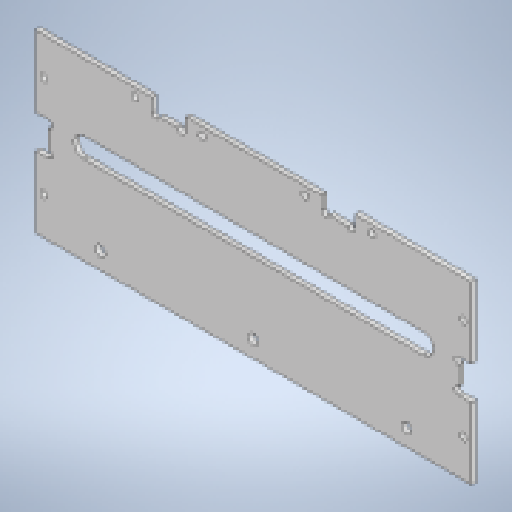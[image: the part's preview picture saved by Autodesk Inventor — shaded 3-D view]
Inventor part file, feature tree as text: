
AUTODESK INVENTOR PART (.ipt)
format: ipt  version: 2024 (Build 280153000, 153)  size: 256,000 bytes
history: native  units: mm
features: other x6, extrude x4, sketch x4, reference x3, projected_geometry x1
ambient origin geometry x8: Origin, YZ Plane, XZ Plane, XY Plane, X Axis, Y Axis, Z Axis, Center Point
bodies: Body1 (feature_tree)
feature tree (18):
  other  "ソリッド1"
  extrude  "押し出し1"  Depth=6.0mm
  extrude  "押し出し2"  Depth=20.0mm
  extrude  "押し出し3"  Depth=10.0mm
  extrude  "押し出し4"  Depth=10.0mm
  sketch  "スケッチ1"
  reference  "参照1"
  reference  "参照2"
  sketch  "スケッチ2"
  projected_geometry  "投影ループ1"
  sketch  "スケッチ3"
  reference  "参照3"
  sketch  "スケッチ4"
  other  "<userpath>\OneDrive\ドキュメント\Inventor\Vixen\leg.iam"
  other  "leg.iam"
  other  "SR3-100_On:1"
  other  "01029_01042_LowheightServoHorn:1"
  other  "sukima:1"
